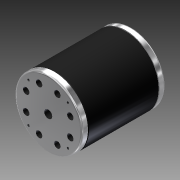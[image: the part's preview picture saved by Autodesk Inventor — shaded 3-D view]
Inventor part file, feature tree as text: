
AUTODESK INVENTOR PART (.ipt)
format: ipt  version: 2012 (Build 160160000, 160)  size: 187,392 bytes
history: native  units: in
note: dims shown in document units (in); Inventor stores cm internally (conversion verified against a paired STEP export)
features: other x3, sketch x3
ambient origin geometry x8: Origin, YZ Plane, XZ Plane, XY Plane, X Axis, Y Axis, Z Axis, Center Point
bodies: Solid1 (feature_tree)
feature tree (6):
  other  "my1020_motor.ipt"
  other  "Solid1::my1020_motor.ipt"
  sketch  "Sketch1"  dims[d0=0.3937in]
  sketch  "Sketch6"
  sketch  "Sketch7"
  other  "TaggingFeature1"
